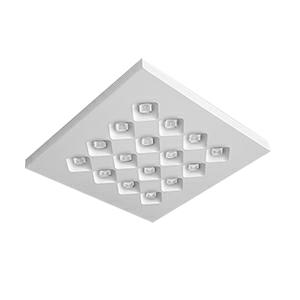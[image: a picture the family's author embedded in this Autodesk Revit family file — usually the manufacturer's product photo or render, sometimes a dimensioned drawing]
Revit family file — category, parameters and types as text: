
# Revit family: 3f_filippi_-_3f_diagon_3f_filippi_-_23106_a0686_-_3f_diagon_25w-930_ep_596x596___corn_plaf__3265
name_source: partatom
category: Lighting Fixtures
units: mm (PartAtom-declared; Revit-internal decimal feet)

## family parameters
Cut with Voids When Loaded = No
Host = Face
Light Source = No
Part Type = Normal
Room Calculation Point = No
Round Connector Dimension = Use Diameter
Shared = No

## types (1)
- 3F Filippi - 3F Dìagon (1 x LED, 3103 lm, 29 W, 3000 K)
    Apparent Load = 29 VA
    Approval mark = ENEC
    CIE Flux Codes = 67 96 100 100 100
    Color Rendering = 90
    Color Temperature = 3000 K
    Control Gear = Electronic ballast
    Default Elevation = 1800 mm
    Description = ILLUMINOTECHNICAL
Luminous efficiency 100% (DLOR 100%, ULOR 0%).
Initial luminous flux of the luminaire 3103 lm.
Emergency luminaire luminous flux BLF 19.8%.
Direct symmetric distribution.
Installation Interdistance Transv.D = 1.39 x hu - Long.D = 1.39 x hu.
Average luminance <1500 cd/m² for radial angles >65°.
Tabular UGR (CIE 117 - 4H-8H; S=0.25H; 70/50/20): RUG 16.3 - 16.2.
Beam angle: 93° - 92°.
Luminous efficacy 107 lm/W.
Lifetime (L95/B10): 30000 h. (tq+25°C)
Lifetime (L90/B10): 50000 h. (tq+25°C)
Lifetime (L80/B10): 80000 h. (tq+25°C)
Lifetime (L75/B10): 100000 h. (tq+25°C)
Sudden decreased luminous flux after 50000 hours: 0% (C0).
Photobiological safety in compliance with IEC/TR 62778: RG0 risk exempt, (IEC 62471).
In compliance with IEC/EN 62722-2-1 - IEC/EN 62717 standards.

SOURCE
Squared LED module 25W/930.
Energy efficiency class (UE 2019/2020 - UE 2019/2015): E.
CIE 13.3 Colour rendering index: CRI >90 (R9 >50%).
IES TM-30 Fidelity Index: Rf = 92 Rg = 101.
CCT nominal colour temperature 3000 K.
Colour initial tolerance (MacAdam): SDCM 3.

MECHANICAL
Housing in hot-galvanised steel, painted in white polyester.
Honeycombed diagonal screen in white anti-glare polycarbonate.
Rhomboidal lenses with differentiated surfaces, etched and prismatic to optimise the orientation of the luminous flux, in transparent methacrylate (PMMA).
Luminaire with limited surface temperature. - D - (EN 60598-2-24)
Dimensions: 600x600 mm, height 40 mm. Weight 6.985 kg.
IP43 protection degree for exposed part, IP20 for recessed part.
Mechanical strength to impacts IK06 (1 joule).
Glow-wire test resistance 650°C.

ELECTRICAL
Halogen Free electronic wiring 230V-50/60Hz, power factor 0.90, THD <25%, constant output current, class I, 1 driver.
Power of the luminaire 29 W.
CE - IEC 60598-1 - EN 60598-1.
EP maintained emergency wiring on board, 1h duration, 24h recharge; compliant with EN 60598-2-22, excluding high risk areas.
SAFE FLICKER: PstLM=<1 and SVM=<0.4 (IEC TR 61547-1 and IEC TR 63158), to ensure a more comfortable and safe light.
Ambient temperature from +5°C to +25°C.
Temperature class T6 max 85°C.
Quick connection.
Relative humidity UR: <85%.

INSTALLATION
Ceiling.
Height only 40 mm.
All accessories dedicated to this product are available on the Catalog and on our website www.3F-Filippi.com.

ACCESSORIES
A0686 - 596x596 Diagon frame for Ceiling installation.

APPLICATIONS
Environments: staterooms, with VDTs, offices.
Environments with exacting visual tasks, where diffused soft light for optimum visual comfort is required.

WARNING
Luminaire designed for disposal/recycling at end-of-life.
Replaceable (LED only) light source by a professional. Replaceable control gear by a professional.
    Height = 0 mm  [stored 0 ft]
    Lamp = 1 x LED
    Lamp Light Flux = 3103 lm
    Lamp Power = 29 W
    Lamp count = 1
    Length = 600 mm
    Lifetime = 50000 h
    Luminous efficacy = 107 lm/W
    Manufacturer = 3F Filippi
    ModVariant = No
    Model = 3F Filippi - 23106+A0686 - 3F Diagon 25W-930 EP 596x596 + Corn.plaf.
    Mounting Place = Ceiling
    Mounting Type = Recessed
    Number of Poles = 1
    OnlyDefault = Yes
    Power Factor = 1
    Product Name = 3F Filippi - 3F Dìagon
    Product group = recessed luminaire
    ProductGroupID = 4
    Protection Class = Protection class I
    Protection Degree = IP 20
    RLX_Detail_Level = 1
    RLX_Emergency_Light_Flux = 0 lm
    RLX_Emergency_Type = 0
    RLX_Emergency_Type_DB = No
    RlxData = <blob elided: 95857 chars, md5=aa0bcfa6>
    Socket = socket
    Standby Power = 0 W
    System Light Flux = 3103 lm
    System Power = 29 W
    Type Comments = Product without accessories
    Type Image = 3ffilippi_3f_diagon__a0686.jpg
    URL = http://relux.com
    VarID = ---
    Voltage = 0 V
    Weight = 0.00 kg
    Width = 600 mm

note: [stored X ft] marks values corroborated as IEEE doubles in the binary element streams (Revit-internal decimal feet)

## geometry (parser evidence)
native form markers: Blend x4, Sweep x10
no freeform markers — native parametric forms only
